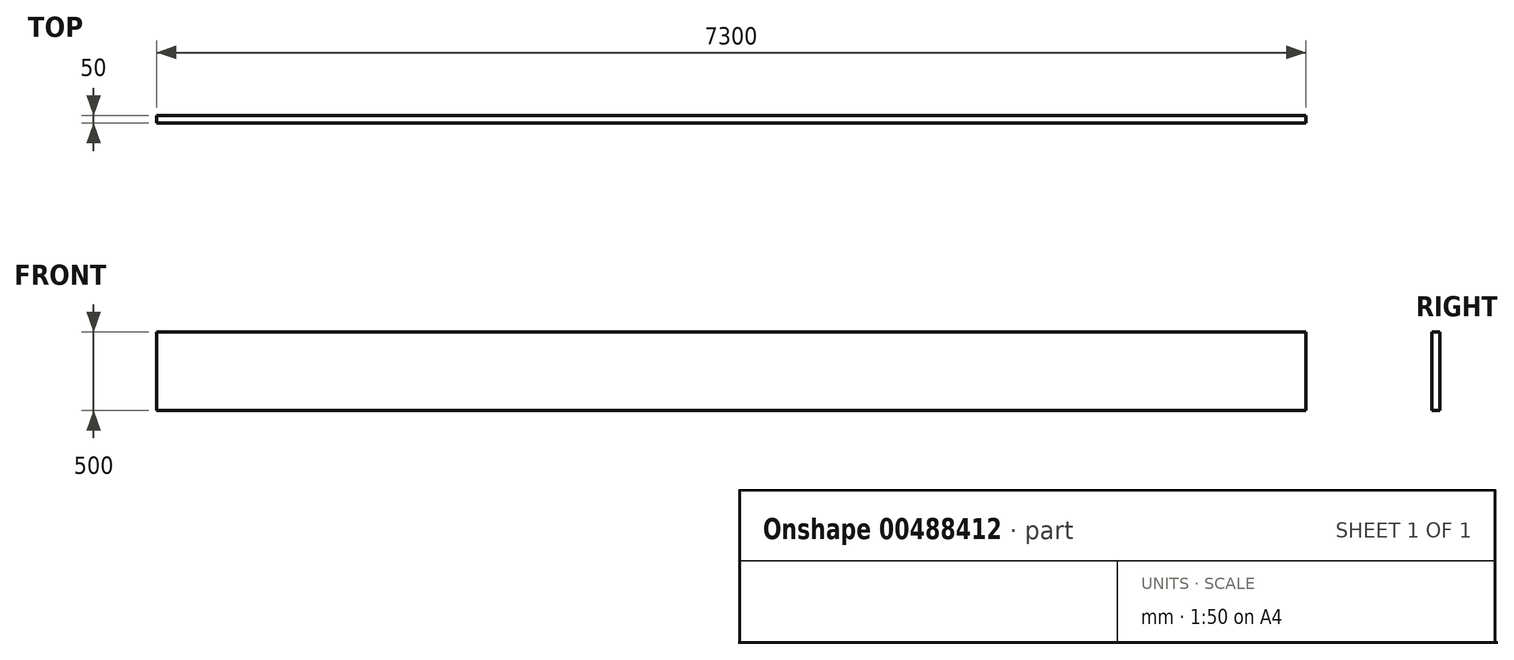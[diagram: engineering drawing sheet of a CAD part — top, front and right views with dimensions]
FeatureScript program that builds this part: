
annotation { "Feature Type Name" : "Feature", "Feature Type Description" : "" }
export const myFeature = defineFeature(function(context is Context, id is Id, definition is map)
    precondition{}
    {
        {
            var Q0;
            Q0=qCreatedBy(makeId("Front.planeOp"),FACE);
            var sketch = newSketch(context, id + "F0", { "sketchPlane" : qUnion([Q0])});
            skLineSegment(sketch, "E0.bottom", {"start": v(3650, -250) * mm, "end": v(-3650, -250) * mm});
            skLineSegment(sketch, "E0.top", {"start": v(3650, 250) * mm, "end": v(-3650, 250) * mm});
            skLineSegment(sketch, "E0.left", {"start": v(3650, -250) * mm, "end": v(3650, 250) * mm});
            skLineSegment(sketch, "E0.right", {"start": v(-3650, -250) * mm, "end": v(-3650, 250) * mm});
            skPoint(sketch, "E0.middle", {"position": v(0, 0) * mm});
            skSolve(sketch);
        }
        {
            var Q0;
            Q0=makeQuery(id+"F0.imprint","IMPRINT",FACE,{"disambiguationData":[TD([[makeQuery(id+"F0.imprint","IMPRINT",EDGE,{"derivedFrom":sQuery(id+"F0.wireOp",EDGE,"E0.bottom")}),-1.0]])]});
            extrude(context, id + "F1", {"entities" : qUnion([Q0]), "endBound" : BoundingType.SYMMETRIC, "depth" : 50 * mm});
        }
    });
